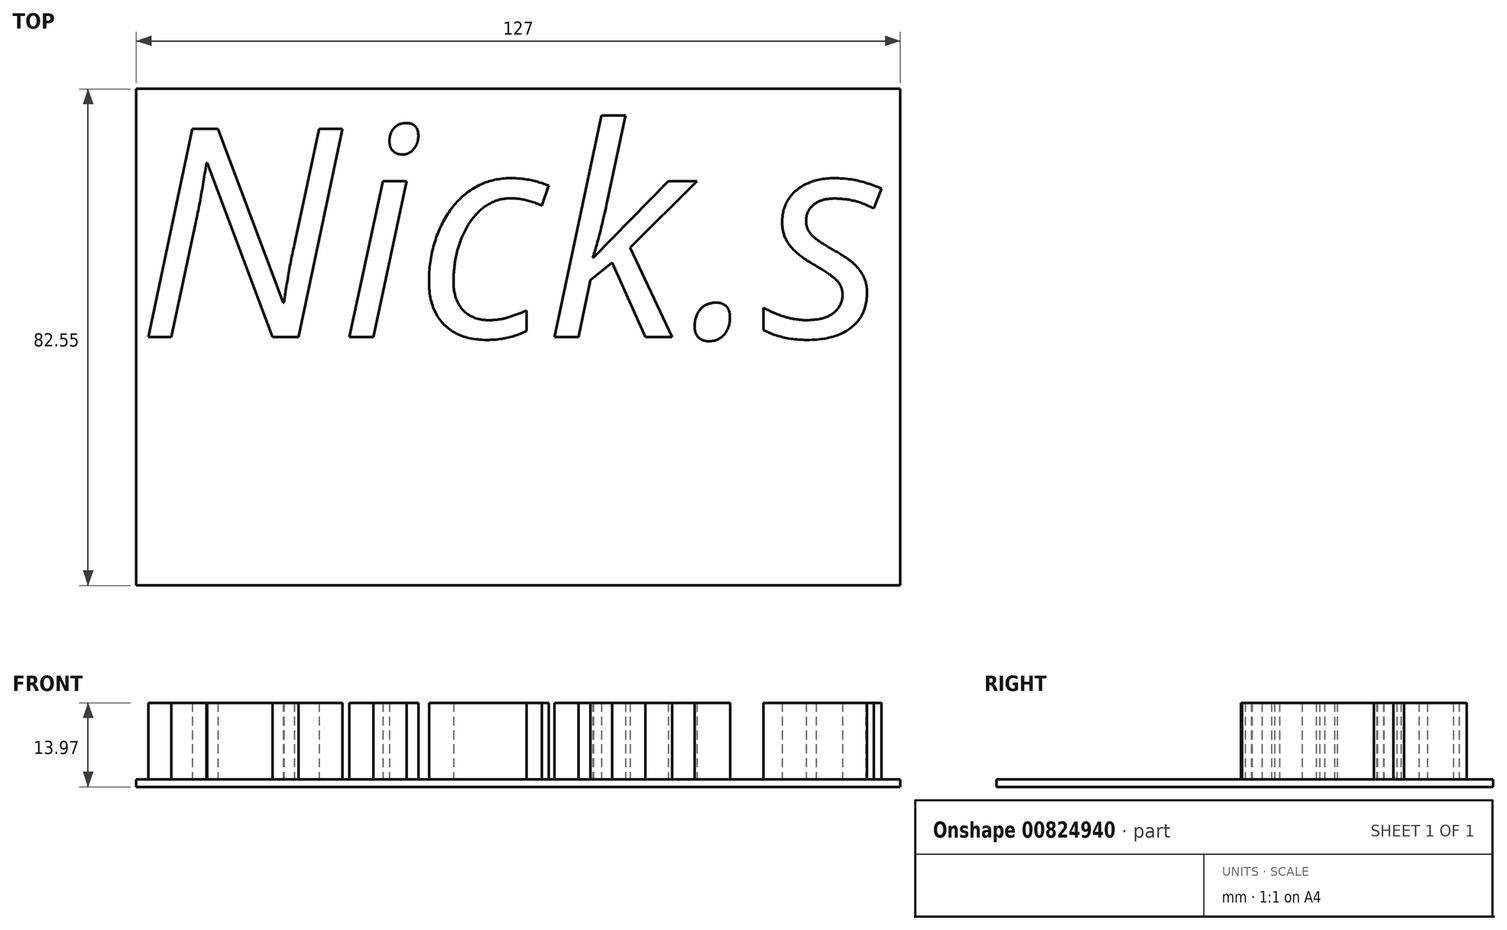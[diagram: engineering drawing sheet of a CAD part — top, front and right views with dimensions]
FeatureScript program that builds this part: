
annotation { "Feature Type Name" : "Feature", "Feature Type Description" : "" }
export const myFeature = defineFeature(function(context is Context, id is Id, definition is map)
    precondition{}
    {
        {
            var Q0;
            Q0=qCreatedBy(makeId("Top.planeOp"),FACE);
            var sketch = newSketch(context, id + "F0", { "sketchPlane" : qUnion([Q0])});
            skLineSegment(sketch, "E0", {"start": v(-76.48, -24.45) * mm, "end": v(50.52, -24.45) * mm});
            skLineSegment(sketch, "E1", {"start": v(50.52, -24.45) * mm, "end": v(50.52, 51.75) * mm});
            skLineSegment(sketch, "E2", {"start": v(50.52, 51.75) * mm, "end": v(-76.48, 51.75) * mm});
            skLineSegment(sketch, "E3", {"start": v(-76.48, 51.75) * mm, "end": v(-76.48, -24.45) * mm});
            skSolve(sketch);
        }
        {
            var Q0;
            Q0=makeQuery(id+"F0.imprint","IMPRINT",FACE,{"disambiguationData":[TD([[makeQuery(id+"F0.imprint","IMPRINT",EDGE,{"derivedFrom":sQuery(id+"F0.wireOp",EDGE,"E0")}),1.0]])]});
            extrude(context, id + "F1", {"entities" : qUnion([Q0]), "depth" : 1.27 * mm, "offsetDistance" : 25.4 * mm});
        }
        {
            var Q0;
            Q0=makeQuery(id+"F1.opExtrude","CAP_FACE",FACE,{"disambiguationData":[OSD([sQuery(id+"F0.wireOp",EDGE,"E0"),sQuery(id+"F0.wireOp",EDGE,"E1"),sQuery(id+"F0.wireOp",EDGE,"E2"),sQuery(id+"F0.wireOp",EDGE,"E3")])],"isStart":false});
            var sketch = newSketch(context, id + "F2", { "sketchPlane" : qUnion([Q0])});
            skText(sketch, "E4", { "text": "Nick.s", "fontName": "OpenSans-Italic.ttf"});
            const initialGuessF2  = {"E4": [-0.07648, 0.01685, 1, 0, 0.0349]};
            skSetInitialGuess(sketch, initialGuessF2);
            skSolve(sketch);
        }
        {
            var Q0;
            Q0 = qSketchRegion(id + "F2", true);
            extrude(context, id + "F3", {"entities" : qUnion([Q0]), "operationType" : NewBodyOperationType.ADD, "depth" : 12.7 * mm, "offsetDistance" : 25.4 * mm});
        }
        {
            var Q0;
            Q0=makeQuery(id+"F1.opExtrude","CAP_FACE",FACE,{"disambiguationData":[OSD([sQuery(id+"F0.wireOp",EDGE,"E0"),sQuery(id+"F0.wireOp",EDGE,"E1"),sQuery(id+"F0.wireOp",EDGE,"E2"),sQuery(id+"F0.wireOp",EDGE,"E3")])],"isStart":false});
            var sketch = newSketch(context, id + "F4", { "sketchPlane" : qUnion([Q0])});
            skLineSegment(sketch, "E5", {"start": v(50.52, 51.75) * mm, "end": v(50.52, 58.1) * mm});
            skLineSegment(sketch, "E6", {"start": v(50.52, 58.1) * mm, "end": v(-76.48, 58.1) * mm});
            skLineSegment(sketch, "E7", {"start": v(-76.48, 58.1) * mm, "end": v(-76.48, 51.75) * mm});
            skSolve(sketch);
        }
        {
            var Q0;
            Q0=makeQuery(id+"F4.imprint","IMPRINT",FACE,{"disambiguationData":[TD([[makeQuery(id+"F4.imprint","IMPRINT",EDGE,{"derivedFrom":sQuery(id+"F4.wireOp",EDGE,"E5")}),1.0]])]});
            extrude(context, id + "F5", {"entities" : qUnion([Q0]), "operationType" : NewBodyOperationType.ADD, "oppositeDirection" : true, "depth" : 1.27 * mm, "offsetDistance" : 25.4 * mm});
        }
    });
